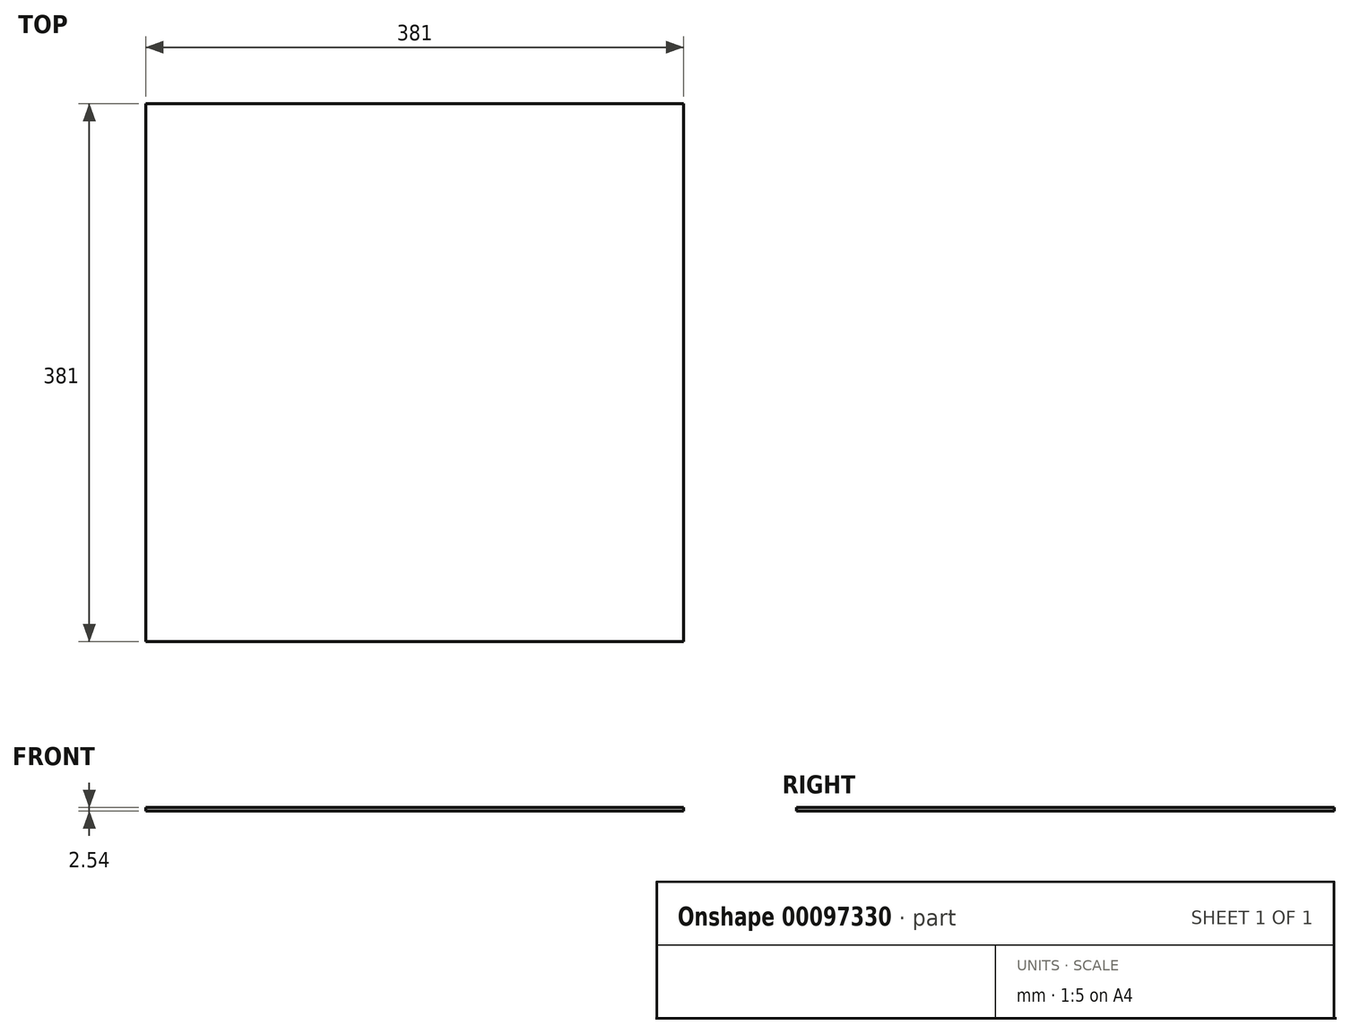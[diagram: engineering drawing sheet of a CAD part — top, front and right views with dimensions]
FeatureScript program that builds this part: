
annotation { "Feature Type Name" : "Feature", "Feature Type Description" : "" }
export const myFeature = defineFeature(function(context is Context, id is Id, definition is map)
    precondition{}
    {
        {
            var Q0;
            Q0=qCreatedBy(makeId("Top.planeOp"),FACE);
            var sketch = newSketch(context, id + "F0", { "sketchPlane" : qUnion([Q0])});
            skLineSegment(sketch, "E0.bottom", {"start": v(190.5, 190.5) * mm, "end": v(-190.5, 190.5) * mm});
            skLineSegment(sketch, "E0.top", {"start": v(190.5, -190.5) * mm, "end": v(-190.5, -190.5) * mm});
            skLineSegment(sketch, "E0.left", {"start": v(190.5, 190.5) * mm, "end": v(190.5, -190.5) * mm});
            skLineSegment(sketch, "E0.right", {"start": v(-190.5, 190.5) * mm, "end": v(-190.5, -190.5) * mm});
            skPoint(sketch, "E0.middle", {"position": v(0, 0) * mm});
            skSolve(sketch);
        }
        {
            var Q0;
            Q0=makeQuery(id+"F0.imprint","IMPRINT",FACE,{"disambiguationData":[TD([[makeQuery(id+"F0.imprint","IMPRINT",EDGE,{"derivedFrom":sQuery(id+"F0.wireOp",EDGE,"E0.bottom")}),1.0]])]});
            extrude(context, id + "F1", {"entities" : qUnion([Q0]), "depth" : 2.54 * mm});
        }
    });
